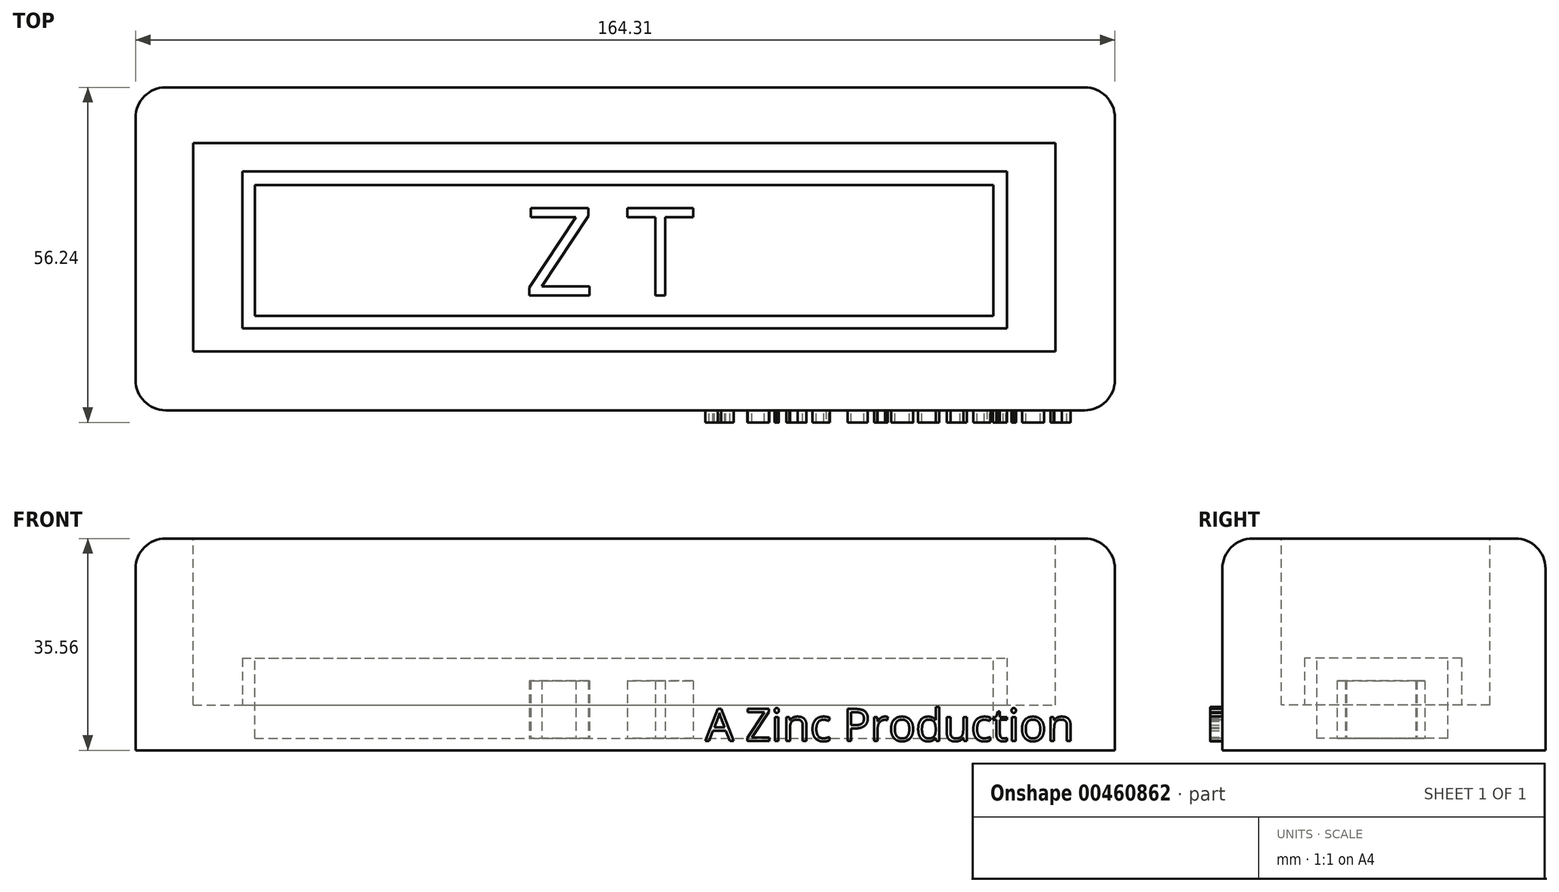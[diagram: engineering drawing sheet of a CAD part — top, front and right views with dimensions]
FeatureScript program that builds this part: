
annotation { "Feature Type Name" : "Feature", "Feature Type Description" : "" }
export const myFeature = defineFeature(function(context is Context, id is Id, definition is map)
    precondition{}
    {
        {
            var Q0;
            Q0=qCreatedBy(makeId("Top.planeOp"),FACE);
            var sketch = newSketch(context, id + "F0", { "sketchPlane" : qUnion([Q0])});
            skLineSegment(sketch, "E0.bottom", {"start": v(-107.44, 20.14) * mm, "end": v(56.87, 20.14) * mm});
            skLineSegment(sketch, "E0.top", {"start": v(-107.44, -34.07) * mm, "end": v(56.87, -34.07) * mm});
            skLineSegment(sketch, "E0.left", {"start": v(-107.44, 20.14) * mm, "end": v(-107.44, -34.07) * mm});
            skLineSegment(sketch, "E0.right", {"start": v(56.87, 20.14) * mm, "end": v(56.87, -34.07) * mm});
            skSolve(sketch);
        }
        {
            var Q0;
            Q0 = qSketchRegion(id + "F0", true);
            extrude(context, id + "F1", {"entities" : qUnion([Q0]), "depth" : 35.56 * mm});
        }
        {
            var Q0;
            Q0=makeQuery(id+"F1.opExtrude","CAP_EDGE",EDGE,{"disambiguationData":[OSD([sQuery(id+"F0.wireOp",EDGE,"E0.left")])],"isStart":false});
            var Q1;
            Q1=makeQuery(id+"F1.opExtrude","CAP_EDGE",EDGE,{"disambiguationData":[OSD([sQuery(id+"F0.wireOp",EDGE,"E0.bottom")])],"isStart":false});
            var Q2;
            Q2=makeQuery(id+"F1.opExtrude","CAP_EDGE",EDGE,{"disambiguationData":[OSD([sQuery(id+"F0.wireOp",EDGE,"E0.right")])],"isStart":false});
            var Q3;
            Q3=makeQuery(id+"F1.opExtrude","CAP_EDGE",EDGE,{"disambiguationData":[OSD([sQuery(id+"F0.wireOp",EDGE,"E0.top")])],"isStart":false});
            var Q4;
            Q4=makeQuery(id+"F1.opExtrude","SWEPT_EDGE",EDGE,{"disambiguationData":[OSD([sQuery(id+"F0.wireOp",EDGE,"E0.top"),sQuery(id+"F0.wireOp",EDGE,"E0.right")])]});
            var Q5;
            Q5=makeQuery(id+"F1.opExtrude","SWEPT_EDGE",EDGE,{"disambiguationData":[OSD([sQuery(id+"F0.wireOp",EDGE,"E0.bottom"),sQuery(id+"F0.wireOp",EDGE,"E0.right")])]});
            var Q6;
            Q6=makeQuery(id+"F1.opExtrude","SWEPT_EDGE",EDGE,{"disambiguationData":[OSD([sQuery(id+"F0.wireOp",EDGE,"E0.top"),sQuery(id+"F0.wireOp",EDGE,"E0.left")])]});
            var Q7;
            Q7=makeQuery(id+"F1.opExtrude","SWEPT_EDGE",EDGE,{"disambiguationData":[OSD([sQuery(id+"F0.wireOp",EDGE,"E0.bottom"),sQuery(id+"F0.wireOp",EDGE,"E0.left")])]});
            fillet(context, id + "F2", {"entities" : qUnion([Q0, Q1, Q2, Q3, Q4, Q5, Q6, Q7]), "radius" : 5.08 * mm, "tangentPropagation" : true, "allowEdgeOverflow" : false});
        }
        {
            var Q0;
            Q0=makeQuery(id+"F1.opExtrude","CAP_FACE",FACE,{"disambiguationData":[OSD([sQuery(id+"F0.wireOp",EDGE,"E0.bottom"),sQuery(id+"F0.wireOp",EDGE,"E0.top"),sQuery(id+"F0.wireOp",EDGE,"E0.left"),sQuery(id+"F0.wireOp",EDGE,"E0.right")])],"isStart":false});
            var sketch = newSketch(context, id + "F3", { "sketchPlane" : qUnion([Q0])});
            skLineSegment(sketch, "E1.bottom", {"start": v(-97.8, 10.81) * mm, "end": v(46.9, 10.81) * mm});
            skLineSegment(sketch, "E1.top", {"start": v(-97.8, -24.18) * mm, "end": v(46.9, -24.18) * mm});
            skLineSegment(sketch, "E1.left", {"start": v(-97.8, 10.81) * mm, "end": v(-97.8, -24.18) * mm});
            skLineSegment(sketch, "E1.right", {"start": v(46.9, 10.81) * mm, "end": v(46.9, -24.18) * mm});
            skSolve(sketch);
        }
        {
            var Q0;
            Q0 = qSketchRegion(id + "F3", true);
            extrude(context, id + "F4", {"entities" : qUnion([Q0]), "operationType" : NewBodyOperationType.REMOVE, "oppositeDirection" : true, "depth" : 27.94 * mm});
        }
        {
            var Q0;
            Q0=makeQuery(id+"F1.opExtrude","SWEPT_FACE",FACE,{"disambiguationData":[OSD([sQuery(id+"F0.wireOp",EDGE,"E0.top")])]});
            var sketch = newSketch(context, id + "F5", { "sketchPlane" : qUnion([Q0])});
            skText(sketch, "E2", { "text": "A Zinc Production", "fontName": "OpenSans-Regular.ttf"});
            const initialGuessF5  = {"E2": [-0.01186, 0.00155, 1, 0, 0.00543]};
            skSetInitialGuess(sketch, initialGuessF5);
            skSolve(sketch);
        }
        {
            var Q0;
            Q0 = qSketchRegion(id + "F5", true);
            extrude(context, id + "F6", {"entities" : qUnion([Q0]), "operationType" : NewBodyOperationType.ADD, "depth" : 2.03 * mm});
        }
        {
            var Q0;
            Q0=makeQuery(id+"F4.boolean.opBoolean","COPY",FACE,{"derivedFrom":makeQuery(id+"F4.opExtrude","CAP_FACE",FACE,{"disambiguationData":[OSD([sQuery(id+"F3.wireOp",EDGE,"E1.bottom"),sQuery(id+"F3.wireOp",EDGE,"E1.top"),sQuery(id+"F3.wireOp",EDGE,"E1.left"),sQuery(id+"F3.wireOp",EDGE,"E1.right")])],"isStart":false})});
            var sketch = newSketch(context, id + "F7", { "sketchPlane" : qUnion([Q0])});
            skLineSegment(sketch, "E3.bottom", {"start": v(-89.54, 6.04) * mm, "end": v(38.78, 6.04) * mm});
            skLineSegment(sketch, "E3.top", {"start": v(-89.54, -20.3) * mm, "end": v(38.78, -20.3) * mm});
            skLineSegment(sketch, "E3.left", {"start": v(-89.54, 6.04) * mm, "end": v(-89.54, -20.3) * mm});
            skLineSegment(sketch, "E3.right", {"start": v(38.78, 6.04) * mm, "end": v(38.78, -20.3) * mm});
            skSolve(sketch);
        }
        {
            var Q0;
            Q0 = qSketchRegion(id + "F7", true);
            extrude(context, id + "F8", {"entities" : qUnion([Q0]), "operationType" : NewBodyOperationType.ADD, "depth" : 7.87 * mm});
        }
        {
            var Q0;
            Q0=makeQuery(id+"F8.opExtrude","CAP_FACE",FACE,{"disambiguationData":[OSD([sQuery(id+"F7.wireOp",EDGE,"E3.bottom"),sQuery(id+"F7.wireOp",EDGE,"E3.top"),sQuery(id+"F7.wireOp",EDGE,"E3.left"),sQuery(id+"F7.wireOp",EDGE,"E3.right")])],"isStart":false});
            var sketch = newSketch(context, id + "F9", { "sketchPlane" : qUnion([Q0])});
            skLineSegment(sketch, "E4.bottom", {"start": v(-87.43, 3.76) * mm, "end": v(36.47, 3.76) * mm});
            skLineSegment(sketch, "E4.top", {"start": v(-87.43, -18.2) * mm, "end": v(36.47, -18.2) * mm});
            skLineSegment(sketch, "E4.left", {"start": v(-87.43, 3.76) * mm, "end": v(-87.43, -18.2) * mm});
            skLineSegment(sketch, "E4.right", {"start": v(36.47, 3.76) * mm, "end": v(36.47, -18.2) * mm});
            skSolve(sketch);
        }
        {
            var Q0;
            Q0 = qSketchRegion(id + "F9", true);
            extrude(context, id + "F10", {"entities" : qUnion([Q0]), "operationType" : NewBodyOperationType.REMOVE, "oppositeDirection" : true, "depth" : 13.46 * mm});
        }
        {
            var Q0;
            Q0=makeQuery(id+"F10.boolean.opBoolean","COPY",FACE,{"derivedFrom":makeQuery(id+"F10.opExtrude","CAP_FACE",FACE,{"disambiguationData":[OSD([sQuery(id+"F9.wireOp",EDGE,"E4.bottom"),sQuery(id+"F9.wireOp",EDGE,"E4.top"),sQuery(id+"F9.wireOp",EDGE,"E4.left"),sQuery(id+"F9.wireOp",EDGE,"E4.right")])],"isStart":false})});
            var sketch = newSketch(context, id + "F11", { "sketchPlane" : qUnion([Q0])});
            skText(sketch, "E5", { "text": "Z T", "fontName": "OpenSans-Regular.ttf"});
            const initialGuessF11  = {"E5": [-0.04218, -0.01481, 1, 0, 0.01481]};
            skSetInitialGuess(sketch, initialGuessF11);
            skSolve(sketch);
        }
        {
            var Q0;
            Q0 = qSketchRegion(id + "F11", true);
            extrude(context, id + "F12", {"entities" : qUnion([Q0]), "operationType" : NewBodyOperationType.ADD, "depth" : 9.65 * mm});
        }
    });
